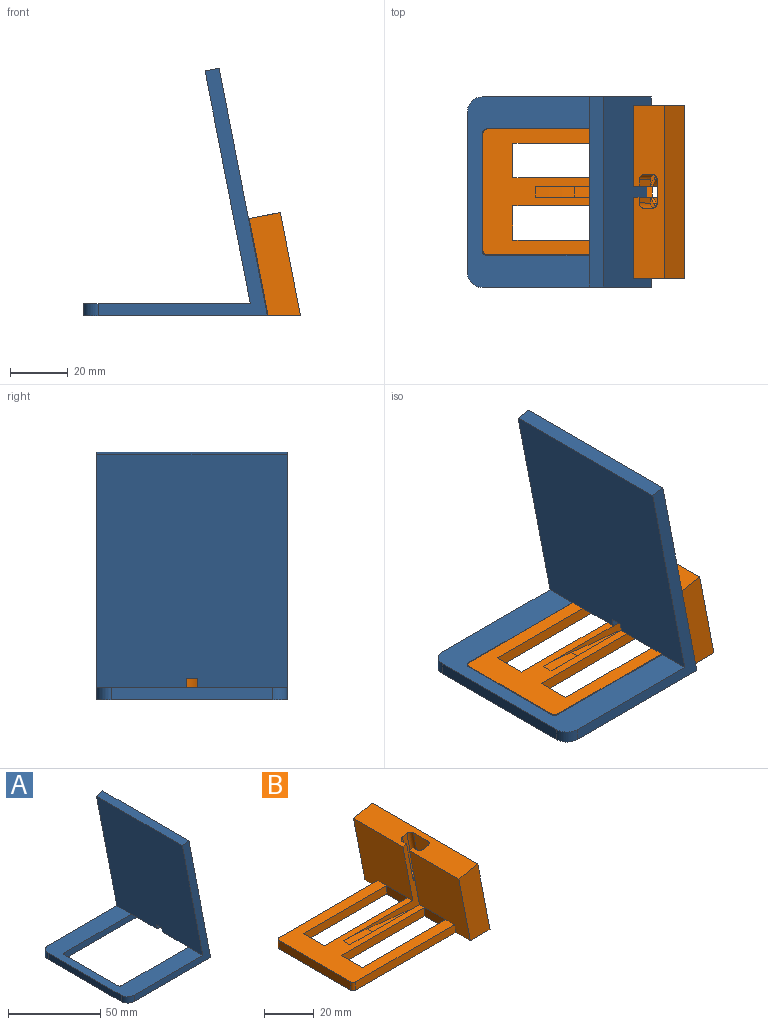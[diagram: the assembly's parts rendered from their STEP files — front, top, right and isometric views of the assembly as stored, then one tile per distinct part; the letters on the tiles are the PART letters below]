
ASSEMBLY  parts=2 mates=1
PART A: 20 faces, bbox 63.7x66x85.9 mm
  f0: plane 80.74x66mm, normal (-0.98,0,-0.19), area 5407.4mm2, adj f1,f2,f3,f4,f7,f9,f10,f16
  f1: plane 19.92x5.09mm, normal (0,0,-1), area 101.4mm2, adj f0,f5,f9,f18
  f2: plane 66x57.79mm, normal (0,0,1), area 1495mm2, adj f0,f3,f4,f8,f9,f10,f11,f12
  f3: plane 85.89x58.7mm, normal (0,-1,0), area 658.5mm2, adj f0,f2,f5,f6,f12,f16
  f4: plane 85.89x58.7mm, normal (0,1,0), area 658.5mm2, adj f0,f2,f5,f6,f13,f16
  f5: plane 85.89x66mm, normal (0.98,0,0.19), area 5562.5mm2, adj f1,f3,f4,f6,f7,f9,f10,f16
  f6: plane 66x63.7mm, normal (0,0,-1), area 1626mm2, adj f3,f4,f5,f8,f9,f10,f11,f12
  f7: plane 19.92x5.09mm, normal (0,0,-1), area 101.4mm2, adj f0,f5,f10,f19
  f8: plane 40.83x4.2mm, normal (1,0,0), area 171.5mm2, adj f2,f6,f14,f15
  f9: plane 57.1x4.4mm, normal (0,-1,0), area 239.1mm2, adj f0,f1,f2,f5,f6,f14
  f10: plane 57.1x4.4mm, normal (0,1,0), area 239.1mm2, adj f0,f2,f5,f6,f7,f15
  f11: plane 56x4.2mm, normal (-1,0,0), area 235.2mm2, adj f2,f6,f12,f13
  f12: cylinder r=5mm len=5mm, axis (0,0,1), area 33mm2, adj f2,f3,f6,f11
  f13: cylinder r=5mm len=5mm, axis (0,0,-1), area 33mm2, adj f2,f4,f6,f11
  f14: cylinder r=1.5mm len=4.2mm, axis (0,0,1), area 9.9mm2, adj f2,f6,f8,f9
  f15: cylinder r=1.5mm len=4.2mm, axis (0,0,-1), area 9.9mm2, adj f2,f6,f8,f10
  f16: plane 66x4.91mm, normal (-0.19,0,0.98), area 330mm2, adj f0,f3,f4,f5
  f17: plane 4.91x4mm, normal (0.19,0,-0.98), area 20mm2, adj f0,f5,f18,f19
  f18: plane 5.67x3.93mm, normal (0,-1,0), area 17.6mm2, adj f0,f1,f5,f17
  f19: plane 5.67x3.93mm, normal (0,1,0), area 17.6mm2, adj f0,f5,f7,f17
PART B: 49 faces, bbox 69.9x60x36.3 mm
  f0: plane 69.87x60.05mm, normal (0,0,-1), area 2040.6mm2, adj f3,f4,f7,f8,f9,f10,f11,f12
  f1: plane 57.8x43.6mm, normal (0,0,1), area 1230.9mm2, adj f3,f7,f8,f11,f12,f13,f28,f29
  f2: plane 6.28x5.51mm, normal (-0.19,0,0.98), area 8.3mm2, adj f13,f14,f15,f18,f21,f22,f31,f32
  f3: plane 57.12x4.2mm, normal (0,1,0), area 238.2mm2, adj f0,f1,f7,f29
  f4: plane 35.75x17.75mm, normal (0,-1,0), area 388.8mm2, adj f0,f6,f8,f10
  f5: plane 6.28x5.51mm, normal (-0.19,0,0.98), area 8.6mm2, adj f12,f16,f17,f18,f19,f20,f35,f36
  f6: plane 60x10.8mm, normal (-0.19,0,0.98), area 579.1mm2, adj f4,f7,f8,f9,f10,f12,f13,f14
  f7: plane 33.65x28.1mm, normal (-0.98,0,-0.19), area 878.1mm2, adj f0,f1,f3,f6,f9,f13,f43
  f8: plane 33.65x28.1mm, normal (-0.98,0,-0.19), area 878.1mm2, adj f0,f1,f4,f6,f11,f12,f41
  f9: plane 35.75x17.75mm, normal (0,1,0), area 388.8mm2, adj f0,f6,f7,f10
  f10: plane 60x35.75mm, normal (0.98,0,0.19), area 2185mm2, adj f0,f4,f6,f9
  f11: plane 57.12x4.2mm, normal (0,-1,0), area 238.2mm2, adj f0,f1,f8,f30
  f12: plane 43.53x34.05mm, normal (0,1,0), area 153.6mm2, adj f0,f1,f5,f6,f8,f16,f23,f37
  f13: plane 43.47x34.05mm, normal (0,-1,0), area 152.8mm2, adj f0,f1,f2,f6,f7,f14,f25,f31
  f14: plane 19.93x3.87mm, normal (0.98,0,0.19), area 45mm2, adj f2,f6,f13,f22
  f15: plane 20.41x6.36mm, normal (0,-1,0), area 51.5mm2, adj f2,f6,f21,f22
  f16: plane 19.93x3.87mm, normal (0.98,0,0.19), area 41mm2, adj f5,f6,f12,f19
  f17: plane 20.41x6.36mm, normal (0,1,0), area 51.5mm2, adj f5,f6,f19,f20
  f18: plane 19.93x8.04mm, normal (-0.98,0,-0.19), area 163.2mm2, adj f2,f5,f6,f20,f21,f34
  f19: cylinder r=1.93mm len=20.3mm, axis (0.19,0,-0.98), area 61.6mm2, adj f5,f6,f16,f17
  f20: cylinder r=1.93mm len=20.3mm, axis (-0.19,0,0.98), area 61.6mm2, adj f5,f6,f17,f18
  f21: cylinder r=1.93mm len=20.3mm, axis (0.19,0,-0.98), area 61.6mm2, adj f2,f6,f15,f18
  f22: cylinder r=1.93mm len=20.3mm, axis (-0.19,0,0.98), area 61.6mm2, adj f2,f6,f14,f15
  f23: cylinder r=6.73mm len=13.98mm, axis (-0.19,0,0.98), area 31.7mm2, adj f0,f12,f26,f37
  f24: cylinder r=1.35mm len=14.75mm, axis (-0.19,0,0.98), area 47.2mm2, adj f0,f25,f27,f32
  f25: cylinder r=6.73mm len=13.99mm, axis (-0.19,0,0.98), area 34.6mm2, adj f0,f13,f24,f31
  f26: cylinder r=1.41mm len=14.75mm, axis (-0.19,0,0.98), area 45.1mm2, adj f0,f23,f27,f36
  f27: cylinder r=7.23mm len=14.73mm, axis (-0.19,0,0.98), area 125.2mm2, adj f0,f24,f26,f33,f34,f35
  f28: plane 40.6x4.2mm, normal (-1,0,0), area 170.5mm2, adj f0,f1,f29,f30
  f29: cylinder r=1.5mm len=4.2mm, axis (0,0,1), area 9.9mm2, adj f0,f1,f3,f28
  f30: cylinder r=1.5mm len=4.2mm, axis (0,0,1), area 9.9mm2, adj f0,f1,f11,f28
  f31: torus R=7.46mm, axis (-0.19,0,0.98), area 3mm2, adj f2,f13,f25,f32
  f32: torus R=2.07mm, axis (-0.19,0,0.98), area 4.4mm2, adj f2,f24,f31,f33
  f33: torus R=7.96mm, axis (-0.19,0,0.98), area 4.5mm2, adj f2,f27,f32,f34
  f34: bspline ~2.14x0.86mm, area 0.9mm2, adj f18,f27,f33,f35
  f35: torus R=7.96mm, axis (-0.19,0,0.98), area 4.5mm2, adj f5,f27,f34,f36
  f36: torus R=2.13mm, axis (-0.19,0,0.98), area 4.2mm2, adj f5,f26,f35,f37
  f37: torus R=7.46mm, axis (-0.19,0,0.98), area 2.7mm2, adj f5,f12,f23,f36
  f38: cylinder r=57.78mm len=6.62mm, axis (0,-1,0), area 25.5mm2, adj f0,f12,f13,f48
  f39: cylinder r=106.23mm len=13.67mm, axis (0,1,0), area 52.1mm2, adj f1,f12,f13,f48
  f40: plane 47.4x4.2mm, normal (0,1,0), area 199.1mm2, adj f0,f1,f41,f42
  f41: plane 12x4.2mm, normal (-1,0,0), area 50.4mm2, adj f0,f8,f40,f47
  f42: plane 12x4.2mm, normal (1,0,0), area 50.4mm2, adj f0,f1,f40,f47
  f43: plane 12x4.2mm, normal (-1,0,0), area 50.4mm2, adj f0,f7,f44,f46
  f44: plane 47.4x4.2mm, normal (0,-1,0), area 199.1mm2, adj f0,f1,f43,f45
  f45: plane 12x4.2mm, normal (1,0,0), area 50.4mm2, adj f0,f1,f44,f46
  f46: plane 47.4x4.2mm, normal (0,1,0), area 199.1mm2, adj f0,f1,f43,f45
  f47: plane 47.4x4.2mm, normal (0,-1,0), area 199.1mm2, adj f0,f1,f41,f42
  f48: cylinder r=623.57mm len=20.18mm, axis (0,1,0), area 77.2mm2, adj f12,f13,f38,f39
PLACE A at identity
PLACE B t=(86.75,-2.86,0.11)mm
MATE parallel B.f1 <-> A.f6  axis (0,0,1) through (16.93,-32.86,4.31)mm
